# Revit family: PA_Арматура трубопроводов [Регулирующий узел для подключения радиатора, VT.225K.N]1 - VALTEC
name_source: partatom
category: Арматура трубопроводов
revit_build: Autodesk Revit 2018 (Build: 20180423_1000(x64)
units: mm (PartAtom-declared; Revit-internal decimal feet)

## family parameters
Всегда вертикально = Да
На основе рабочей плоскости = Нет
Общий = Нет
При загрузке вырезать с полостями = Нет
Размер круглого соединителя = Использовать диаметр
Тип детали = Вставляется

## types (2) — shared parameters
1!!!НЕ ИЗМЕНЯТЬ!!! = VT.1000.0.0
10!!!НЕ ИЗМЕНЯТЬ!!! = VT.TE3041.A.024
11!!!НЕ ИЗМЕНЯТЬ!!! = VT.TE3042.0.024
12!!!НЕ ИЗМЕНЯТЬ!!! = VT.TE3042.0.220
13!!!НЕ ИЗМЕНЯТЬ!!! = VT.TE3042.A.220
14!!!НЕ ИЗМЕНЯТЬ!!! = Колпачок
2!!!НЕ ИЗМЕНЯТЬ!!! = VT.1500.0.0
3!!!НЕ ИЗМЕНЯТЬ!!! = VT.3000.0.0
4!!!НЕ ИЗМЕНЯТЬ!!! = VT.5000.0.0
5!!!НЕ ИЗМЕНЯТЬ!!! = VT.5010.0.0
6!!!НЕ ИЗМЕНЯТЬ!!! = VT.AS1000
7!!!НЕ ИЗМЕНЯТЬ!!! = VT.TE3040.0.220
8!!!НЕ ИЗМЕНЯТЬ!!! = VT.TE3040.A.220
9!!!НЕ ИЗМЕНЯТЬ!!! = VT.TE3041.0.024
ADSK_URL документации изделия = https://valtec.ru
ADSK_URL страницы изделия = https://valtec.ru
ADSK_Материал = Сталь, нержавеющая - VALTEC
ME_1!!!НЕ ИЗМЕНЯТЬ!!! = ME_Оборудование [головка термостатическая твердотельная, VT.1000.0] - VALTEC
ME_10!!!НЕ ИЗМЕНЯТЬ!!! = ME_Оборудование [сервопривод электрический, VT.TE3041.A.024] - VALTEC
ME_11!!!НЕ ИЗМЕНЯТЬ!!! = ME_Оборудование [сервопривод электрический, VT.TE3042.0.024] - VALTEC
ME_12!!!НЕ ИЗМЕНЯТЬ!!! = ME_Оборудование [сервопривод электрический, VT.TE3042.0.220] - VALTEC
ME_13!!!НЕ ИЗМЕНЯТЬ!!! = ME_Оборудование [сервопривод электрический, VT.TE3042.A.220] - VALTEC
ME_14!!!НЕ ИЗМЕНЯТЬ!!! = ME_Оборудование [колпачек] - VALTEC
ME_2!!!НЕ ИЗМЕНЯТЬ!!! = ME_Оборудование [головка термостатическая жидкостная, VT.1500.0] - VALTEC
ME_3!!!НЕ ИЗМЕНЯТЬ!!! = ME_Оборудование [головка термостатическая жидкостная, VT.3000.0] - VALTEC
ME_4!!!НЕ ИЗМЕНЯТЬ!!! = ME_Оборудование [головка термостатическая жидкостная, VT.5000.0] - VALTEC
ME_5!!!НЕ ИЗМЕНЯТЬ!!! = ME_Оборудование [головка термостатическая жидкостная, VT.5010.0] - VALTEC
ME_6!!!НЕ ИЗМЕНЯТЬ!!! = ME_Оборудование [cервопривод EQUICALOR, VT.AS1000] - VALTEC
ME_7!!!НЕ ИЗМЕНЯТЬ!!! = ME_Оборудование [сервопривод электрический, VT.TE3040.0.220] - VALTEC
ME_8!!!НЕ ИЗМЕНЯТЬ!!! = ME_Оборудование [сервопривод электрический, VT.TE3040.A.220] - VALTEC
ME_9!!!НЕ ИЗМЕНЯТЬ!!! = ME_Оборудование [сервопривод электрический, VT.TE3041.0.024] - VALTEC
MM_1!!!НЕ ИЗМЕНЯТЬ!!! = MM_Обобщенные модели [головка термостатическая твердотельная, VT.1000.0] - VALTEC : VT.1000.0
MM_2!!!НЕ ИЗМЕНЯТЬ!!! = MM_Обобщенные модели [головка термостатическая жидкостная, VT.1500.0] - VALTEC : VT.1500.0
MM_3!!!НЕ ИЗМЕНЯТЬ!!! = MM_Обобщенные модели [головка термостатическая жидкостная, VT.3000.0] - VALTEC : VT.3000.0
MM_4!!!НЕ ИЗМЕНЯТЬ!!! = MM_Обобщенные модели [головка термостатическая жидкостная, VT.5000.0] - VALTEC : VT.5000.0 - VT.5010.0
MM_5!!!НЕ ИЗМЕНЯТЬ!!! = MM_Обобщенные модели [cервопривод EQUICALOR, VT.AS1000] - VALTEC : VT.AS1000
MM_6!!!НЕ ИЗМЕНЯТЬ!!! = MM_Обобщенные модели [сервопривод электрический, VT.TE3040] - VALTEC : VT.TE3040
MM_7!!!НЕ ИЗМЕНЯТЬ!!! = MM_Обобщенные модели [сервопривод электрический, VT.TE3042] - VALTEC : VT.TE3042.0
MM_8!!!НЕ ИЗМЕНЯТЬ!!! = MM_Обобщенные модели [колпачок, VT.031.N] - VALTEC : VT.TE3042.0
URL = https://valtec.ru
Изготовитель = VALTEC
Материал доп.1 = Черный - VALTEC
Таблица 1 = PA_Арматура трубопроводов [Регулирующий узел для подключения радиатора, VT.225K.N] - VALTEC - Таблица 1
Таблица 2 = PA_Арматура трубопроводов [Регулирующий узел для подключения радиатора, VT.225K.N] - VALTEC - Таблица 2

## per-type parameters (varying)
| type | x!!!НЕ ИЗМЕНЯТЬ!!! |
| VT.225K.N.E04050 | Нет |
| VT.225K.N.E04100 | Да |
